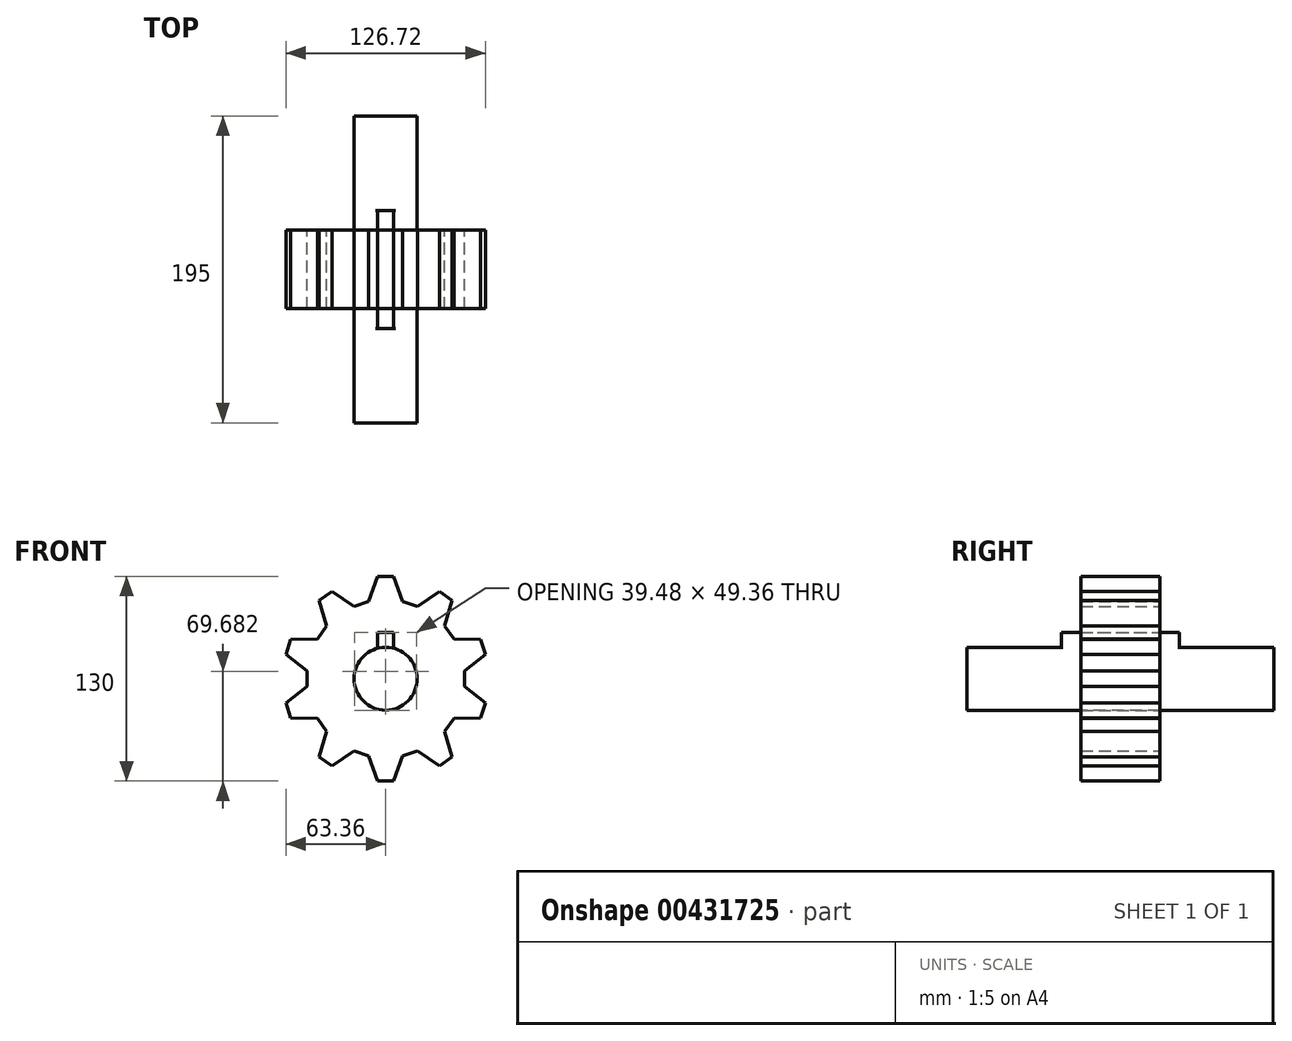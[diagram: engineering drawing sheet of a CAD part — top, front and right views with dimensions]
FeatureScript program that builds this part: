
annotation { "Feature Type Name" : "Feature", "Feature Type Description" : "" }
export const myFeature = defineFeature(function(context is Context, id is Id, definition is map)
    precondition{}
    {
        {
            var Q0;
            Q0=qCreatedBy(makeId("Front.planeOp"),FACE);
            var sketch = newSketch(context, id + "F0", { "sketchPlane" : qUnion([Q0])});
            skCircle(sketch, "E0", {"center": v(0, 0) * mm, "radius": 50 * mm, "construction": true});
            skLineSegment(sketch, "E1", {"start": v(0, -74.5) * mm, "end": v(0, 74) * mm, "construction": true});
            skLineSegment(sketch, "E2", {"start": v(-76.13, 0) * mm, "end": v(86.86, 0) * mm, "construction": true});
            skLineSegment(sketch, "E3", {"start": v(0, 65) * mm, "end": v(5, 65) * mm});
            skLineSegment(sketch, "E4", {"start": v(0, 0) * mm, "end": v(19.12, 58.83) * mm, "construction": true});
            skLineSegment(sketch, "E5", {"start": v(10.7, 49.1) * mm, "end": v(20.2, 46) * mm});
            skPoint(sketch, "E6", {"position": v(15.45, 47.55) * mm});
            skLineSegment(sketch, "E7", {"start": v(5, 65) * mm, "end": v(10.7, 49.1) * mm});
            skLineSegment(sketch, "E8.MirrorCS", {"start": v(34.16, 55.53) * mm, "end": v(20.2, 46) * mm});
            skLineSegment(sketch, "E9.MirrorCS", {"start": v(38.2, 52.59) * mm, "end": v(34.16, 55.53) * mm});
            skLineSegment(sketch, "E10.1.0", {"start": v(-38.2, 52.59) * mm, "end": v(-34.16, 55.53) * mm});
            skLineSegment(sketch, "E10.1.1", {"start": v(-34.16, 55.53) * mm, "end": v(-20.2, 46) * mm});
            skLineSegment(sketch, "E10.1.2", {"start": v(-20.2, 46) * mm, "end": v(-10.7, 49.1) * mm});
            skLineSegment(sketch, "E10.1.3", {"start": v(-5, 65) * mm, "end": v(-10.7, 49.1) * mm});
            skLineSegment(sketch, "E10.1.4", {"start": v(0, 65) * mm, "end": v(-5, 65) * mm});
            skLineSegment(sketch, "E10.2.0", {"start": v(-61.82, 20.09) * mm, "end": v(-60.27, 24.84) * mm});
            skLineSegment(sketch, "E10.2.1", {"start": v(-60.27, 24.84) * mm, "end": v(-43.39, 25.34) * mm});
            skLineSegment(sketch, "E10.2.2", {"start": v(-43.39, 25.34) * mm, "end": v(-37.51, 33.43) * mm});
            skLineSegment(sketch, "E10.2.3", {"start": v(-42.25, 49.65) * mm, "end": v(-37.51, 33.43) * mm});
            skLineSegment(sketch, "E10.2.4", {"start": v(-38.2, 52.59) * mm, "end": v(-42.25, 49.65) * mm});
            skLineSegment(sketch, "E10.3.0", {"start": v(-61.82, -20.09) * mm, "end": v(-63.36, -15.33) * mm});
            skLineSegment(sketch, "E10.3.1", {"start": v(-63.36, -15.33) * mm, "end": v(-50, -5) * mm});
            skLineSegment(sketch, "E10.3.2", {"start": v(-50, -5) * mm, "end": v(-50, 5) * mm});
            skLineSegment(sketch, "E10.3.3", {"start": v(-63.36, 15.33) * mm, "end": v(-50, 5) * mm});
            skLineSegment(sketch, "E10.3.4", {"start": v(-61.82, 20.09) * mm, "end": v(-63.36, 15.33) * mm});
            skLineSegment(sketch, "E10.4.0", {"start": v(-38.2, -52.59) * mm, "end": v(-42.25, -49.65) * mm});
            skLineSegment(sketch, "E10.4.1", {"start": v(-42.25, -49.65) * mm, "end": v(-37.51, -33.43) * mm});
            skLineSegment(sketch, "E10.4.2", {"start": v(-37.51, -33.43) * mm, "end": v(-43.39, -25.34) * mm});
            skLineSegment(sketch, "E10.4.3", {"start": v(-60.27, -24.84) * mm, "end": v(-43.39, -25.34) * mm});
            skLineSegment(sketch, "E10.4.4", {"start": v(-61.82, -20.09) * mm, "end": v(-60.27, -24.84) * mm});
            skLineSegment(sketch, "E10.5.0", {"start": v(0, -65) * mm, "end": v(-5, -65) * mm});
            skLineSegment(sketch, "E10.5.1", {"start": v(-5, -65) * mm, "end": v(-10.7, -49.1) * mm});
            skLineSegment(sketch, "E10.5.2", {"start": v(-10.7, -49.1) * mm, "end": v(-20.2, -46) * mm});
            skLineSegment(sketch, "E10.5.3", {"start": v(-34.16, -55.53) * mm, "end": v(-20.2, -46) * mm});
            skLineSegment(sketch, "E10.5.4", {"start": v(-38.2, -52.59) * mm, "end": v(-34.16, -55.53) * mm});
            skLineSegment(sketch, "E10.6.0", {"start": v(38.2, -52.59) * mm, "end": v(34.16, -55.53) * mm});
            skLineSegment(sketch, "E10.6.1", {"start": v(34.16, -55.53) * mm, "end": v(20.2, -46) * mm});
            skLineSegment(sketch, "E10.6.2", {"start": v(20.2, -46) * mm, "end": v(10.7, -49.1) * mm});
            skLineSegment(sketch, "E10.6.3", {"start": v(5, -65) * mm, "end": v(10.7, -49.1) * mm});
            skLineSegment(sketch, "E10.6.4", {"start": v(0, -65) * mm, "end": v(5, -65) * mm});
            skLineSegment(sketch, "E10.7.0", {"start": v(61.82, -20.09) * mm, "end": v(60.27, -24.84) * mm});
            skLineSegment(sketch, "E10.7.1", {"start": v(60.27, -24.84) * mm, "end": v(43.39, -25.34) * mm});
            skLineSegment(sketch, "E10.7.2", {"start": v(43.39, -25.34) * mm, "end": v(37.51, -33.43) * mm});
            skLineSegment(sketch, "E10.7.3", {"start": v(42.25, -49.65) * mm, "end": v(37.51, -33.43) * mm});
            skLineSegment(sketch, "E10.7.4", {"start": v(38.2, -52.59) * mm, "end": v(42.25, -49.65) * mm});
            skLineSegment(sketch, "E10.8.0", {"start": v(61.82, 20.09) * mm, "end": v(63.36, 15.33) * mm});
            skLineSegment(sketch, "E10.8.1", {"start": v(63.36, 15.33) * mm, "end": v(50, 5) * mm});
            skLineSegment(sketch, "E10.8.2", {"start": v(50, 5) * mm, "end": v(50, -5) * mm});
            skLineSegment(sketch, "E10.8.3", {"start": v(63.36, -15.33) * mm, "end": v(50, -5) * mm});
            skLineSegment(sketch, "E10.8.4", {"start": v(61.82, -20.09) * mm, "end": v(63.36, -15.33) * mm});
            skLineSegment(sketch, "E10.9.0", {"start": v(38.2, 52.59) * mm, "end": v(42.25, 49.65) * mm});
            skLineSegment(sketch, "E10.9.1", {"start": v(42.25, 49.65) * mm, "end": v(37.51, 33.43) * mm});
            skLineSegment(sketch, "E10.9.2", {"start": v(37.51, 33.43) * mm, "end": v(43.39, 25.34) * mm});
            skLineSegment(sketch, "E10.9.3", {"start": v(60.27, 24.84) * mm, "end": v(43.39, 25.34) * mm});
            skLineSegment(sketch, "E10.9.4", {"start": v(61.82, 20.09) * mm, "end": v(60.27, 24.84) * mm});
            skSolve(sketch);
        }
        {
            var Q0;
            Q0=makeQuery(id+"F0.imprint","IMPRINT",FACE,{"disambiguationData":[TD([[makeQuery(id+"F0.imprint","IMPRINT",EDGE,{"derivedFrom":sQuery(id+"F0.wireOp",EDGE,"E3")}),-1.0]])]});
            extrude(context, id + "F1", {"entities" : qUnion([Q0]), "endBound" : BoundingType.SYMMETRIC, "depth" : 50 * mm});
        }
        {
            var Q0;
            Q0=qCreatedBy(makeId("Front.planeOp"),FACE);
            var sketch = newSketch(context, id + "F2", { "sketchPlane" : qUnion([Q0])});
            skArc(sketch, "E11", {"start": v(-6.36, 18.96) * mm, "mid": v(0, -20) * mm, "end": v(6.36, 18.96) * mm});
            skLineSegment(sketch, "E12", {"start": v(-5, 20.86) * mm, "end": v(-5, 29.36) * mm});
            skLineSegment(sketch, "E13", {"start": v(-5, 29.36) * mm, "end": v(5, 29.36) * mm});
            skLineSegment(sketch, "E14", {"start": v(5, 29.36) * mm, "end": v(5, 20.86) * mm});
            skPoint(sketch, "E15", {"position": v(0, 29.36) * mm});
            skPoint(sketch, "E16.visualSharp", {"position": v(5, 19.36) * mm});
            skArc(sketch, "E16.filletArc", {"start": v(5, 20.86) * mm, "mid": v(5.38, 19.69) * mm, "end": v(6.36, 18.96) * mm});
            skPoint(sketch, "E17.visualSharp", {"position": v(-5, 19.36) * mm});
            skArc(sketch, "E17.filletArc", {"start": v(-6.36, 18.96) * mm, "mid": v(-5.38, 19.69) * mm, "end": v(-5, 20.86) * mm});
            skSolve(sketch);
        }
        {
            var Q0;
            Q0 = qSketchRegion(id + "F2", true);
            extrude(context, id + "F3", {"entities" : qUnion([Q0]), "operationType" : NewBodyOperationType.REMOVE, "endBound" : BoundingType.SYMMETRIC, "oppositeDirection" : true, "depth" : 50 * mm});
        }
        {
            var Q0;
            Q0 = qSketchRegion(id + "F2", true);
            extrude(context, id + "F4", {"entities" : qUnion([Q0]), "endBound" : BoundingType.SYMMETRIC, "depth" : 75 * mm});
        }
        {
            var Q0;
            Q0=makeQuery(id+"F4.opExtrude","CAP_FACE",FACE,{"disambiguationData":[OSD([sQuery(id+"F2.wireOp",EDGE,"E11"),sQuery(id+"F2.wireOp",EDGE,"E12"),sQuery(id+"F2.wireOp",EDGE,"E13"),sQuery(id+"F2.wireOp",EDGE,"E14"),sQuery(id+"F2.wireOp",EDGE,"E16.filletArc"),sQuery(id+"F2.wireOp",EDGE,"E17.filletArc")])],"isStart":false});
            var sketch = newSketch(context, id + "F5", { "sketchPlane" : qUnion([Q0])});
            skCircle(sketch, "E18", {"center": v(0, 0) * mm, "radius": 20 * mm});
            skSolve(sketch);
        }
        {
            var Q0;
            {var subQ0=sQuery(id+"F5.wireOp",EDGE,"E18");var subQ1=makeQuery(id+"F5.imprint","INTERSECT",VERTEX,{"derivedFrom":[makeQuery(id+"F4.opExtrude","CAP_EDGE",EDGE,{"disambiguationData":[OSD([sQuery(id+"F2.wireOp",EDGE,"E17.filletArc")])],"isStart":false}),subQ0]});Q0=makeQuery(id+"F5.imprint","IMPRINT",FACE,{"disambiguationData":[TD([[makeQuery(id+"F5.imprint","IMPRINT",EDGE,{"disambiguationData":[TD([[subQ1,-1.0]])],"derivedFrom":subQ0}),1.0]])]});}
            extrude(context, id + "F6", {"entities" : qUnion([Q0]), "depth" : 60 * mm});
        }
        {
            var Q0;
            Q0=makeQuery(id+"F6.opExtrude","SWEPT_BODY",BODY,{"disambiguationData":[OSD([sQuery(id+"F5.wireOp",EDGE,"E18")])]});
            var Q1;
            Q1=qCreatedBy(makeId("Front.planeOp"),FACE);
            mirror(context, id + "F7", {"operationType" : NewBodyOperationType.ADD, "entities" : qUnion([Q0]), "mirrorPlane" : qUnion([Q1])});
        }
    });
